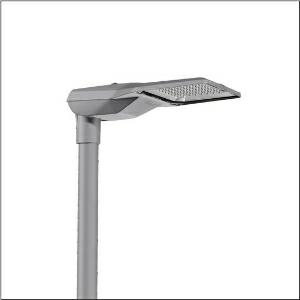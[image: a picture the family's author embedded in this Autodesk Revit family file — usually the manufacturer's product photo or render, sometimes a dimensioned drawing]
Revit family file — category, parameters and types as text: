
# Revit family: streetlight_sl_21_iq_midi___p0_8ab_5xe3r31v08nb_094b
name_source: partatom
category: Lighting Fixtures
units: mm (PartAtom-declared; Revit-internal decimal feet)

## family parameters
Cut with Voids When Loaded = No
Host = Face
Light Source = No
Part Type = Normal
Room Calculation Point = No
Round Connector Dimension = Use Diameter
Shared = No

## types (1)
- --- (1 x LED, 18710 lm, 136.6 W, 3000K)
    Apparent Load = 137 VA
    CIE Flux Codes = 39 72 97 100 100
    Color Rendering = 70
    Color Temperature = 3000K
    Default Elevation = 1800 mm
    Description = Streetlight SL 21 iQ midi, mast luminaire, primary light control with lens, of PMMA, primary optical cover: cover, of toughened safety glass, transparent, light distribution: P0.8aB, light emission: direct distribution, primary light characteristic: asymmetric, installation type: post-top, side-entry, LED, High Power LED, rated luminous flux: 18.710lm, luminous efficacy: 137lm/W, light colour: 730, colour temperature: 3000K, control gear: iQ-Street Remote, D4i with power reduction, control: pre-setting: logarithmic dimming characteristic, Street-Remote, Auto-Match, Temp-Guard, Lumen-Switch, Night-Set, Smart-Wire, Light-Fading, Desk-Remote (wireless, voltage-free reading and setting of iQ features in the workshop via application-optimized NFC function/RFID function), optimised constant luminous flux control (CLO 2.0), mains connection: 230..240V, AC, 50/60Hz, start of lifetime: 137W, end of service life: 144W, reduction: 61W, luminaire housing, of diecast aluminium, powder-coated, Siteco® metallic grey (DB 702S), corrosivity category C5 mid according to DIN EN ISO 12944, please order mast flange separately, inclination adjustable: 0°, 5°, 10°, 15°, sealing non-destructively replaceable, multi-level sealing system, length: 644mm, width: 335mm, height: 110mm, mast flange for spigot size: 42mm (side-entry): 5XC10008XM4, 60/48mm (side-entry/post-top): 5XC10108XM2, 76/60mm (side-entry/post-top): 5XC10108XM1, mounting height: 4..8m, Smart Interface above, protection rating (complete): IP66, insulation class (complete): insulation class II (safety insulation), certification: CE, ENEC, ENEC+, VDE, impact resistance: IK10, permissible operating ambient temperature for outdoor applications: -40..+50°C, standard-compliant lighting for roads and squares, packaging unit: 1 piece

Light Distribution: P0.8aB
    Height = 111 mm
    Lamp = 1 x LED
    Lamp Light Flux = 18710 lm
    Lamp Power = 136.6 W
    Lamp count = 1
    Length = 644 mm
    Luminous efficacy = 137 lm/W
    Manufacturer = Siteco
    ModVariant = No
    Model = 5XE3R31V08NB
    Number of Poles = 1
    OnlyDefault = Yes
    Power Factor = 1
    Product Name = Streetlight SL 21 iQ midi | P0.8aB
    Product group = mast luminaire | pylon top
    ProductGroupID = 6100
    Protection Class = Protection class II
    Protection Degree = IP 66
    RLX_Detail_Level = 1
    RLX_Emergency_Light_Flux = 0 lm
    RLX_Emergency_Type = 0
    RLX_Emergency_Type_DB = No
    RlxData = <blob elided: 26817 chars, md5=7999baff>
    Socket = socket
    Standby Power = 0 W
    System Light Flux = 18710 lm
    System Power = 137 W
    Type Comments = factory setting: luminous flux: 100 % | dim-lin: 254 | 733 mA
    Type Image = l_1004302.jpg
    URL = http://relux.com
    VarID = @adj_071212
    Voltage = 0 V
    Weight = 0.00 kg
    Width = 336 mm

## geometry (parser evidence)
native form markers: Blend x4, Sweep x10
no freeform markers — native parametric forms only
